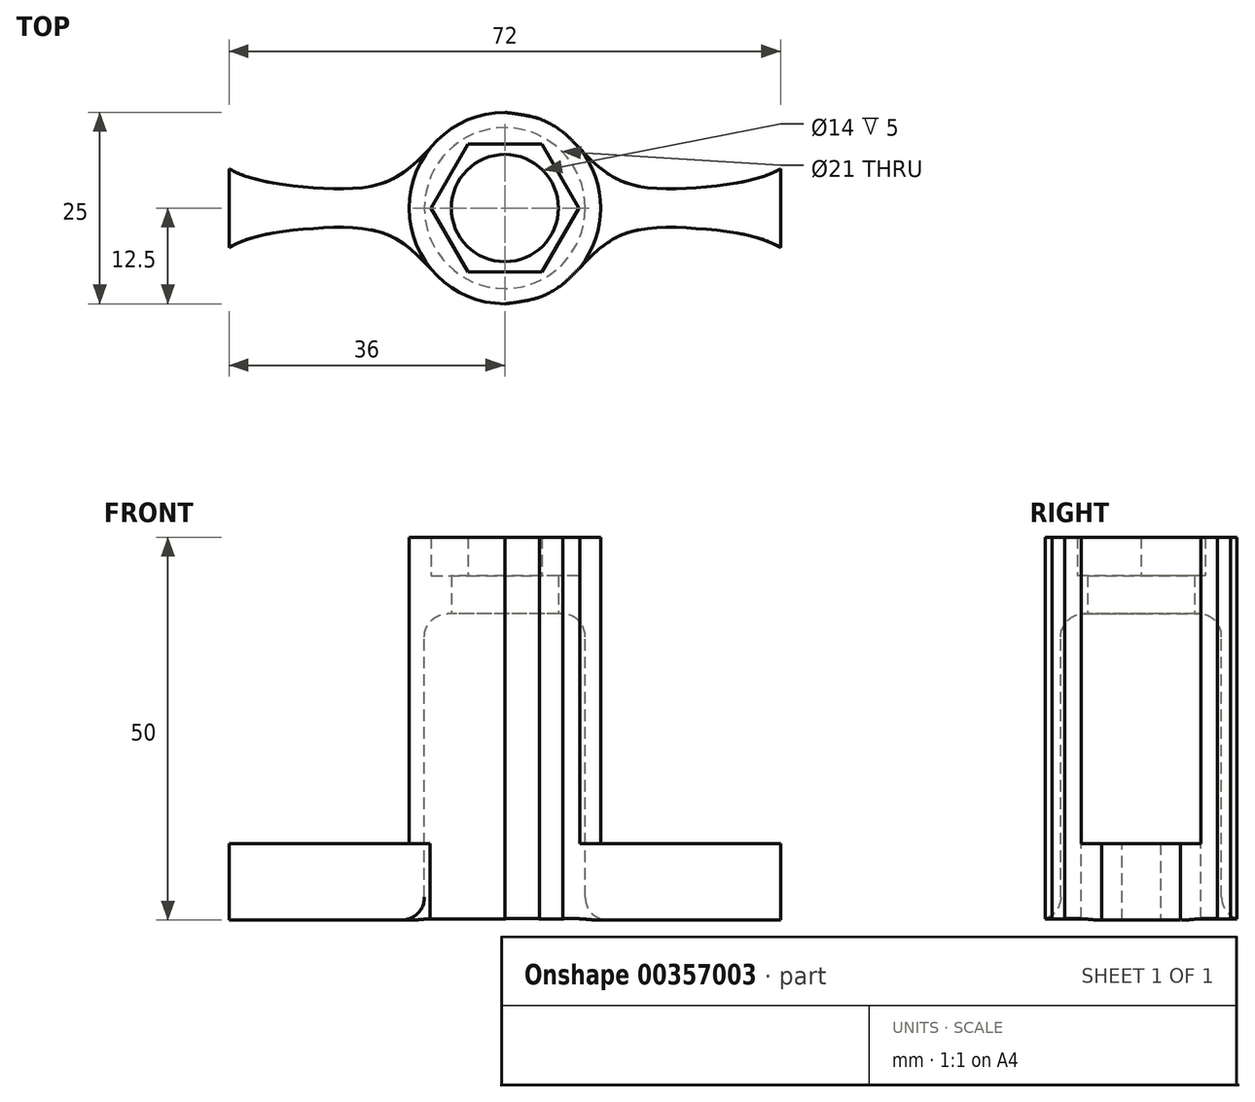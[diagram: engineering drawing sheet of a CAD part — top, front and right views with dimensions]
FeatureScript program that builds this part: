
annotation { "Feature Type Name" : "Feature", "Feature Type Description" : "" }
export const myFeature = defineFeature(function(context is Context, id is Id, definition is map)
    precondition{}
    {
        {
            var Q0;
            Q0=qCreatedBy(makeId("Top.planeOp"),FACE);
            var sketch = newSketch(context, id + "F0", { "sketchPlane" : qUnion([Q0])});
            skCircle(sketch, "E0", {"center": v(0, 0) * mm, "radius": 12.5 * mm});
            skFitSpline(sketch, "E1", {"points": [v(0, 12.5) * mm, v(7.56, 9.96) * mm, v(14.38, 3.93) * mm, v(24.92, 2.66) * mm, v(36, 5.13) * mm], "startDerivative": vector(52.63, -6.31) * mm, "endDerivative": vector(31.65, 18.4) * mm});
            skLineSegment(sketch, "E2", {"start": v(36, 5.13) * mm, "end": v(36, -5.13) * mm});
            skFitSpline(sketch, "E3.MirrorCS", {"points": [v(0, -12.5) * mm, v(7.56, -9.96) * mm, v(14.38, -3.93) * mm, v(24.92, -2.66) * mm, v(36, -5.13) * mm], "startDerivative": vector(52.63, 6.31) * mm, "endDerivative": vector(31.65, -18.4) * mm});
            skCircle(sketch, "E4.cCircle", {"center": v(0, 0) * mm, "radius": 8.35 * mm, "construction": true});
            skLineSegment(sketch, "E4.0", {"start": v(9.64, 0) * mm, "end": v(4.82, -8.35) * mm});
            skLineSegment(sketch, "E4.1", {"start": v(4.82, -8.35) * mm, "end": v(-4.82, -8.35) * mm});
            skLineSegment(sketch, "E4.2", {"start": v(-4.82, -8.35) * mm, "end": v(-9.64, 0) * mm});
            skLineSegment(sketch, "E4.3", {"start": v(-9.64, 0) * mm, "end": v(-4.82, 8.35) * mm});
            skLineSegment(sketch, "E4.4", {"start": v(-4.82, 8.35) * mm, "end": v(4.82, 8.35) * mm});
            skLineSegment(sketch, "E4.5", {"start": v(4.82, 8.35) * mm, "end": v(9.64, 0) * mm});
            skPoint(sketch, "E4.0.midPoint", {"position": v(7.23, -4.18) * mm});
            skCircle(sketch, "E5", {"center": v(0, 0) * mm, "radius": 10.5 * mm});
            skCircle(sketch, "E6", {"center": v(0, 0) * mm, "radius": 7 * mm});
            skSolve(sketch);
        }
        {
            var Q0;
            Q0=makeQuery(id+"F0.imprint","IMPRINT",FACE,{"disambiguationData":[TD([[makeQuery(id+"F0.imprint","IMPRINT",EDGE,{"derivedFrom":sQuery(id+"F0.wireOp",EDGE,"E5")}),-1.0]])]});
            extrude(context, id + "F1", {"entities" : qUnion([Q0]), "oppositeDirection" : true, "depth" : 40 * mm, "hasSecondDirection" : true, "secondDirectionOppositeDirection" : false, "secondDirectionDepth" : 10 * mm});
        }
        {
            var Q0;
            Q0=makeQuery(id+"F0.imprint","IMPRINT",FACE,{"disambiguationData":[TD([[makeQuery(id+"F0.imprint","IMPRINT",EDGE,{"derivedFrom":sQuery(id+"F0.wireOp",EDGE,"E4.0")}),1.0]])]});
            var Q1;
            Q1=makeQuery(id+"F0.imprint","IMPRINT",FACE,{"disambiguationData":[TD([[makeQuery(id+"F0.imprint","IMPRINT",EDGE,{"derivedFrom":sQuery(id+"F0.wireOp",EDGE,"E4.0")}),-1.0]])]});
            extrude(context, id + "F2", {"entities" : qUnion([Q0, Q1]), "operationType" : NewBodyOperationType.ADD, "depth" : 10 * mm});
        }
        {
            var Q0;
            Q0=makeQuery(id+"F0.imprint","IMPRINT",FACE,{"disambiguationData":[TD([[makeQuery(id+"F0.imprint","IMPRINT",EDGE,{"derivedFrom":sQuery(id+"F0.wireOp",EDGE,"E4.0")}),-1.0]])]});
            extrude(context, id + "F3", {"entities" : qUnion([Q0]), "operationType" : NewBodyOperationType.REMOVE, "depth" : 10 * mm, "hasSecondDirection" : true, "secondDirectionOppositeDirection" : false, "secondDirectionDepth" : 5 * mm});
        }
        {
            var Q0;
            {var subQ5=sQuery(id+"F0.wireOp",EDGE,"E2");Q0=makeQuery(id+"F0.imprint","IMPRINT",FACE,{"disambiguationData":[TD([[makeQuery(id+"F0.imprint","IMPRINT",EDGE,{"derivedFrom":subQ5}),-1.0]])]});}
            extrude(context, id + "F4", {"entities" : qUnion([Q0]), "oppositeDirection" : true, "depth" : 40 * mm, "hasSecondDirection" : true, "secondDirectionOppositeDirection" : true, "secondDirectionDepth" : 30 * mm});
        }
        {
            var Q0;
            Q0=makeQuery(id+"F4.opExtrude","SWEPT_BODY",BODY,{"disambiguationData":[OSD([sQuery(id+"F0.wireOp",EDGE,"E0"),sQuery(id+"F0.wireOp",EDGE,"E1"),sQuery(id+"F0.wireOp",EDGE,"E2"),sQuery(id+"F0.wireOp",EDGE,"E3.MirrorCS")])]});
            var Q1;
            Q1=qCreatedBy(makeId("Right.planeOp"),FACE);
            mirror(context, id + "F5", {"operationType" : NewBodyOperationType.ADD, "entities" : qUnion([Q0]), "mirrorPlane" : qUnion([Q1])});
        }
        {
            var Q0;
            Q0=makeQuery(id+"F2.opExtrude","CAP_EDGE",EDGE,{"disambiguationData":[OSD([sQuery(id+"F0.wireOp",EDGE,"E5")])],"isStart":true});
            var Q1;
            Q1=makeQuery(id+"F1.opExtrude","SWEPT_FACE",FACE,{"disambiguationData":[OSD([sQuery(id+"F0.wireOp",EDGE,"E5")])]});
            fillet(context, id + "F6", {"entities" : qUnion([Q0, Q1]), "radius" : 3 * mm, "tangentPropagation" : true, "allowEdgeOverflow" : false});
        }
    });
